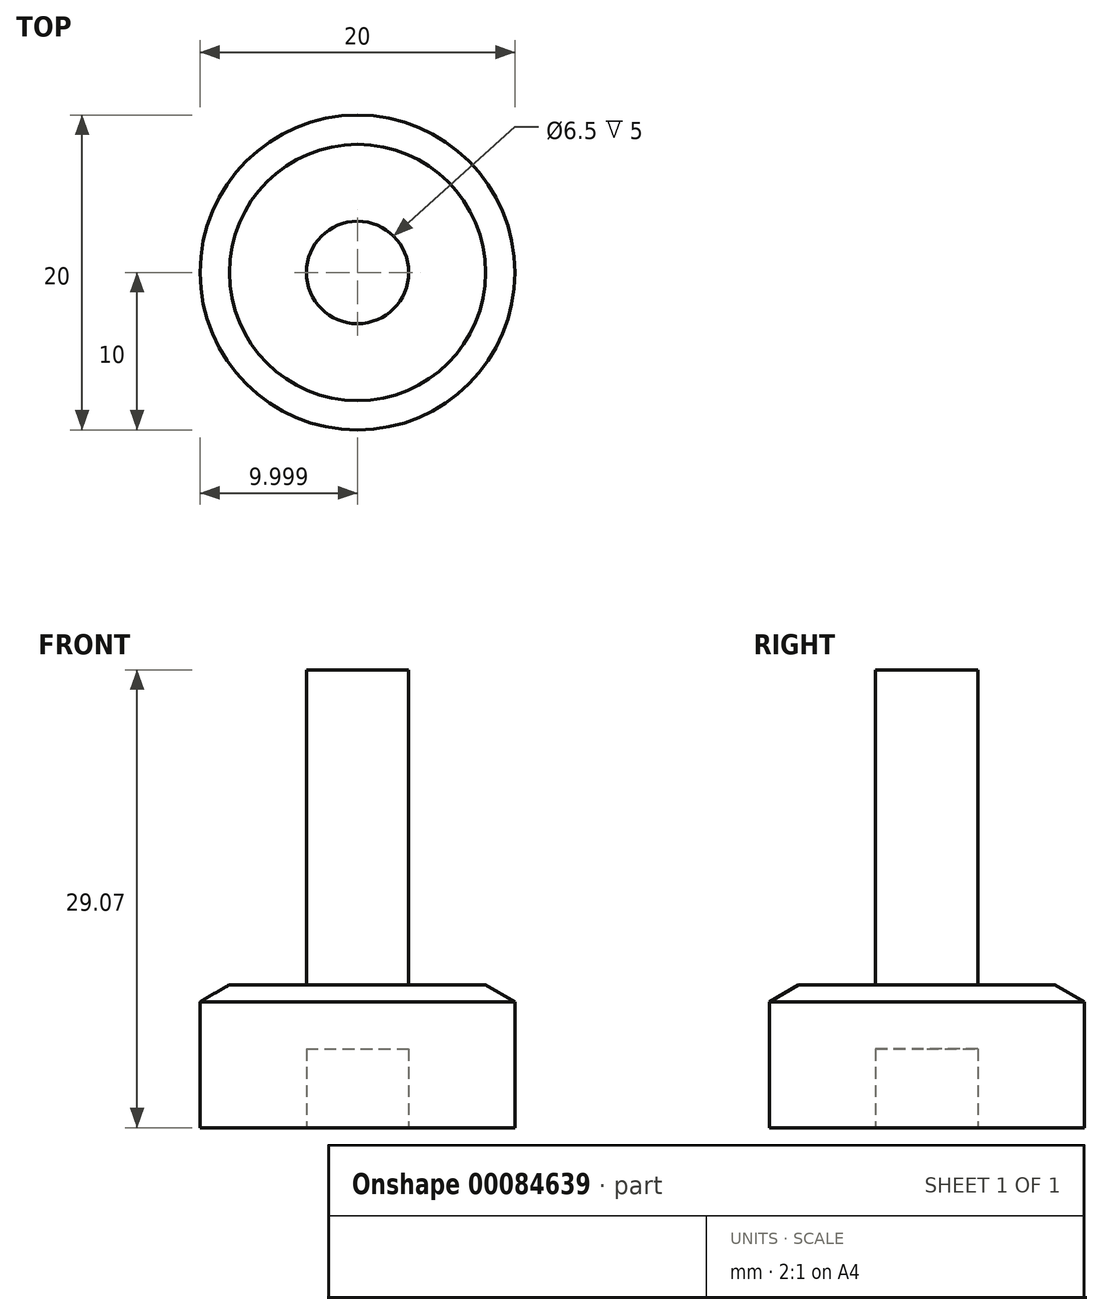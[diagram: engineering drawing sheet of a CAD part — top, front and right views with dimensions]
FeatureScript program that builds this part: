
annotation { "Feature Type Name" : "Feature", "Feature Type Description" : "" }
export const myFeature = defineFeature(function(context is Context, id is Id, definition is map)
    precondition{}
    {
        {
            var Q0;
            Q0=qCreatedBy(makeId("Front.planeOp"),FACE);
            var sketch = newSketch(context, id + "F0", { "sketchPlane" : qUnion([Q0])});
            skLineSegment(sketch, "E0.bottom", {"start": v(-30.55, 8) * mm, "end": v(-20.55, 8) * mm});
            skLineSegment(sketch, "E0.top", {"start": v(-30.55, 0) * mm, "end": v(-23.8, 0) * mm});
            skLineSegment(sketch, "E0.left", {"start": v(-30.55, 8) * mm, "end": v(-30.55, 0) * mm});
            skPoint(sketch, "E1", {"position": v(-20.55, 8) * mm});
            skPoint(sketch, "E2", {"position": v(-20.55, 0) * mm});
            skPoint(sketch, "E3", {"position": v(-20.55, 9.07) * mm});
            skLineSegment(sketch, "E4", {"start": v(-20.55, 8) * mm, "end": v(-20.55, 9.07) * mm});
            skLineSegment(sketch, "E5", {"start": v(-30.55, 8) * mm, "end": v(-28.7, 9.07) * mm});
            skLineSegment(sketch, "E6", {"start": v(-28.7, 9.07) * mm, "end": v(-20.55, 9.07) * mm});
            skLineSegment(sketch, "E7", {"start": v(-20.55, 8) * mm, "end": v(-20.55, 5) * mm});
            skPoint(sketch, "E0.right.end.orphan", {"position": v(-10.55, 0) * mm});
            skPoint(sketch, "E8.start.orphan", {"position": v(-10.55, 8) * mm});
            skLineSegment(sketch, "E9", {"start": v(-20.55, 9.07) * mm, "end": v(-20.55, 29.07) * mm});
            skLineSegment(sketch, "E10", {"start": v(-20.55, 29.07) * mm, "end": v(-23.8, 29.07) * mm});
            skLineSegment(sketch, "E11", {"start": v(-23.8, 29.07) * mm, "end": v(-23.8, 0) * mm});
            skPoint(sketch, "E12.start.orphan", {"position": v(-20.55, 4) * mm});
            skLineSegment(sketch, "E13", {"start": v(-20.55, 5) * mm, "end": v(-23.8, 5) * mm});
            skPoint(sketch, "E14", {"position": v(-20.55, 5) * mm});
            skSolve(sketch);
        }
        {
            var Q0;
            {var subQ0=sQuery(id+"F0.wireOp",EDGE,"E9");Q0=makeQuery(id+"F0.imprint","IMPRINT",FACE,{"disambiguationData":[TD([[makeQuery(id+"F0.imprint","IMPRINT",EDGE,{"derivedFrom":subQ0}),1.0]])]});}
            var Q1;
            {var subQ5=sQuery(id+"F0.wireOp",EDGE,"E0.top");Q1=makeQuery(id+"F0.imprint","IMPRINT",FACE,{"disambiguationData":[TD([[makeQuery(id+"F0.imprint","IMPRINT",EDGE,{"derivedFrom":subQ5}),1.0]])]});}
            var Q2;
            {var subQ0=sQuery(id+"F0.wireOp",EDGE,"E5");Q2=makeQuery(id+"F0.imprint","IMPRINT",FACE,{"disambiguationData":[TD([[makeQuery(id+"F0.imprint","IMPRINT",EDGE,{"derivedFrom":subQ0}),-1.0]])]});}
            var Q3;
            {var subQ0=sQuery(id+"F0.wireOp",EDGE,"E7");Q3=makeQuery(id+"F0.imprint","IMPRINT",FACE,{"disambiguationData":[TD([[makeQuery(id+"F0.imprint","IMPRINT",EDGE,{"derivedFrom":subQ0}),-1.0]])]});}
            var Q4;
            {var subQ0=sQuery(id+"F0.wireOp",EDGE,"E4");Q4=makeQuery(id+"F0.imprint","IMPRINT",FACE,{"disambiguationData":[TD([[makeQuery(id+"F0.imprint","IMPRINT",EDGE,{"derivedFrom":subQ0}),1.0]])]});}
            var Q5;
            Q5=sQuery(id+"F0.wireOp",EDGE,"E9");
            revolve(context, id + "F1", {"entities" : qUnion([Q0, Q1, Q2, Q3, Q4]), "axis" : qUnion([Q5]), "revolveType" : RevolveType.FULL});
        }
    });
